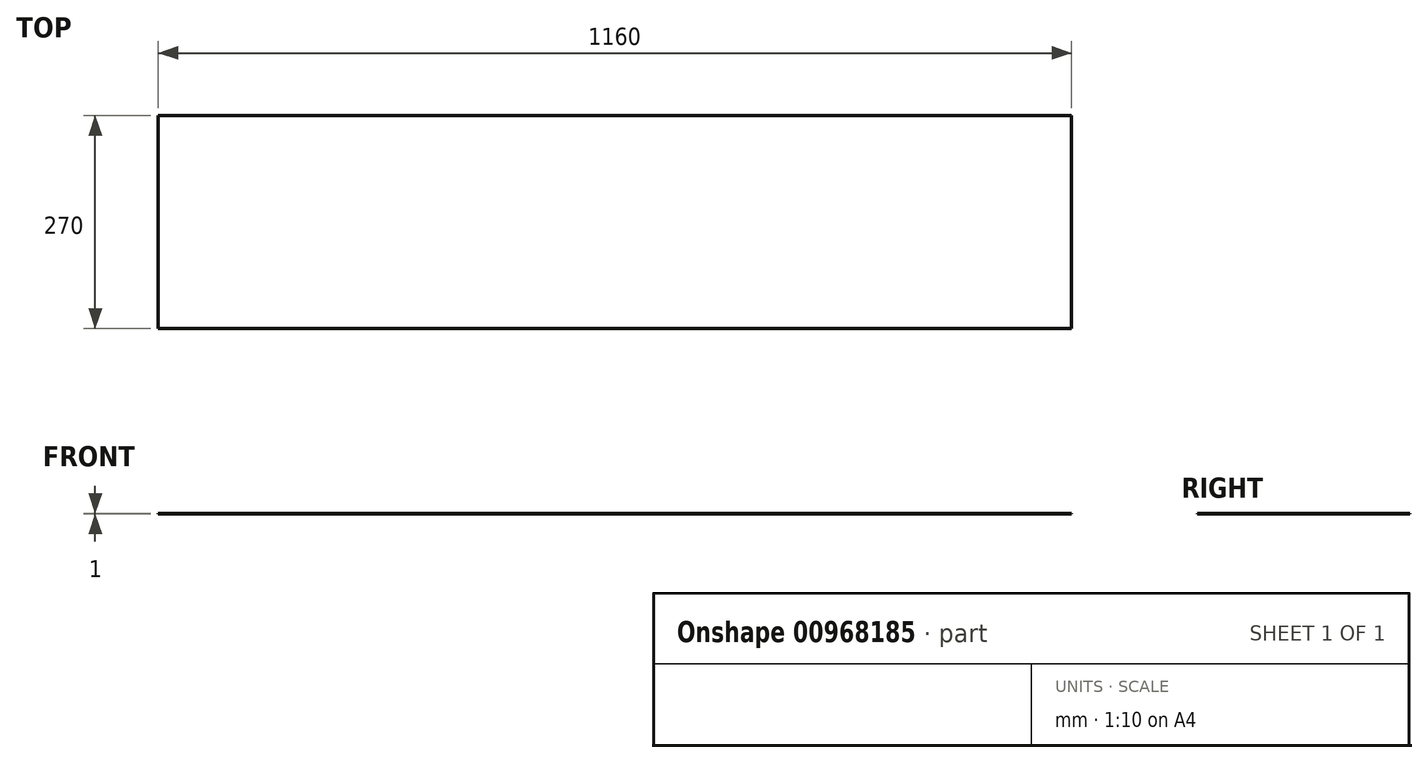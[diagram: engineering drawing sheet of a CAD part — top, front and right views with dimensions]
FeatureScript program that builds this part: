
annotation { "Feature Type Name" : "Feature", "Feature Type Description" : "" }
export const myFeature = defineFeature(function(context is Context, id is Id, definition is map)
    precondition{}
    {
        {
            var Q0;
            Q0=qCreatedBy(makeId("Top.planeOp"),FACE);
            var sketch = newSketch(context, id + "F0", { "sketchPlane" : qUnion([Q0])});
            skLineSegment(sketch, "E0.bottom", {"start": v(0, 0) * mm, "end": v(1160, 0) * mm});
            skLineSegment(sketch, "E0.top", {"start": v(0, 270) * mm, "end": v(1160, 270) * mm});
            skLineSegment(sketch, "E0.left", {"start": v(0, 0) * mm, "end": v(0, 270) * mm});
            skLineSegment(sketch, "E0.right", {"start": v(1160, 0) * mm, "end": v(1160, 270) * mm});
            skSolve(sketch);
        }
        {
            var Q0;
            Q0 = qSketchRegion(id + "F0", true);
            extrude(context, id + "F1", {"entities" : qUnion([Q0]), "depth" : 1 * mm, "offsetDistance" : 25.4 * mm});
        }
    });
